# Revit family: Shower-Valves_and_Controls-KALLISTA-FOUNDATIONS-P29500_1
name_source: partatom
category: Plumbing Fixtures
units: mm (PartAtom-declared; Revit-internal decimal feet)

## family parameters
Cut with Voids When Loaded = No
Host = Face
OmniClass Number = 23.27.31.00
OmniClass Title = Valves
Part Type = Normal
Room Calculation Point = No
Round Connector Dimension = Use Diameter
Shared = No

## types (2) — shared parameters
ADA Compliant = No
Assembly Code = D2020
CW Connection = Yes
Cold Water Inlet = Cold Water Inlet
Date Modified = 08/23/2022
Default Elevation = 42"
Finish = Kallista-Metal-Brass
Flow Rate = 9 GPM
HW Connection = Yes
Height = 5"
Hot Water Inlet = Hot Water Inlet
Length = 4 13/16"
Manufacturer = Kohler Co.
Master Format 2014 = 23 09 13.33
Master Format 2014 Name = Control Valves
Material = Copper Alloy
Pressure = 45.00 psi
Product Name = FOUNDATIONS
Tempered Water Outlet 1 = Tempered Water Outlet 1
Tempered Water Outlet 2 = Tempered Water Outlet 2
URL = https://www.kallista.com
Vent Connection = No
Waste Connection = No
Waste Water Outlet = Waste Water Outlet
WaterSense Certified = No
Width = 4 3/4"

## per-type parameters (varying)
| type | Description | Model | Product Documentation Link | Product Page URL | Type |
| CE Pex With Stops, NA-Brass | ROUGH-IN THERMOSTATIC VLV CE PEX W/STOPS | P29500-US |  |  | 1 |
| Volume Control and Stops, NA-Brass | THERMOSTATIC ROUGH-IN, INTEGRATED VOLUME CONTROL AND STOPS | P29500-WS | https://resources.kohler.com | https://www.kallista.com | 2 |

## geometry (parser evidence)
native form markers: Sweep x3
no freeform markers — native parametric forms only
